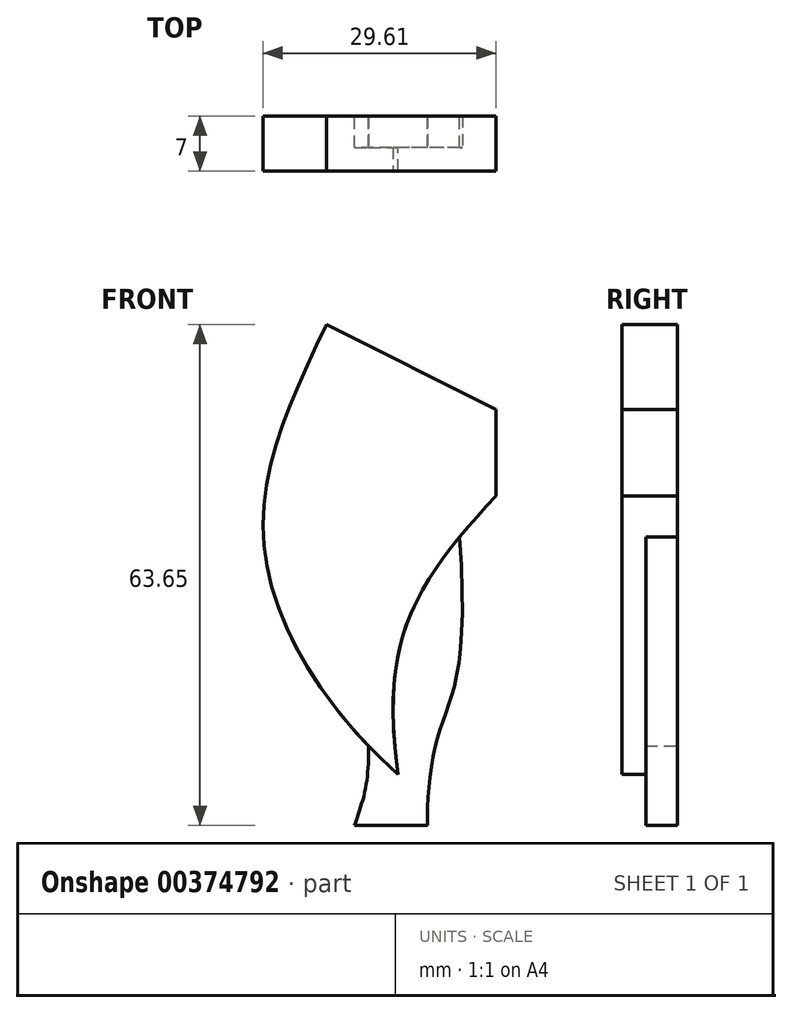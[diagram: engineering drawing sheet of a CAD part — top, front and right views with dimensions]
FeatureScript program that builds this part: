
annotation { "Feature Type Name" : "Feature", "Feature Type Description" : "" }
export const myFeature = defineFeature(function(context is Context, id is Id, definition is map)
    precondition{}
    {
        {
            var Q0;
            Q0=qCreatedBy(makeId("Front.planeOp"),FACE);
            var sketch = newSketch(context, id + "F0", { "sketchPlane" : qUnion([Q0])});
            skLineSegment(sketch, "E0", {"start": v(1.24, 25.64) * mm, "end": v(22.82, 14.85) * mm});
            skLineSegment(sketch, "E1", {"start": v(22.82, 14.85) * mm, "end": v(22.82, 3.84) * mm});
            skFitSpline(sketch, "E2", {"points": [v(1.24, 25.64) * mm, v(-6.63, -2.85) * mm, v(10.35, -31.5) * mm], "startDerivative": vector(-28.14, -59.83) * mm, "endDerivative": vector(50.37, -44.22) * mm});
            skFitSpline(sketch, "E3", {"points": [v(22.82, 3.84) * mm, v(11.92, -11.26) * mm, v(10.35, -31.5) * mm], "startDerivative": vector(-28.02, -29.3) * mm, "endDerivative": vector(6.68, -49.81) * mm});
            skSolve(sketch);
        }
        {
            var Q0;
            Q0 = qSketchRegion(id + "F0", true);
            extrude(context, id + "F1", {"entities" : qUnion([Q0]), "depth" : 7 * mm, "offsetDistance" : 25 * mm});
        }
        {
            var Q0;
            Q0=makeQuery(id+"F1.opExtrude","CAP_FACE",FACE,{"disambiguationData":[OSD([sQuery(id+"F0.wireOp",EDGE,"E0"),sQuery(id+"F0.wireOp",EDGE,"E1"),sQuery(id+"F0.wireOp",EDGE,"E2"),sQuery(id+"F0.wireOp",EDGE,"E3")])],"isStart":true});
            var sketch = newSketch(context, id + "F2", { "sketchPlane" : qUnion([Q0])});
            skFitSpline(sketch, "E4", {"points": [v(-18.16, -1.37) * mm, v(-15.45, -26.61) * mm, v(-14.13, -38.01) * mm], "startDerivative": vector(-6.58, -89.09) * mm, "endDerivative": vector(-1.28, -24.69) * mm});
            skLineSegment(sketch, "E5", {"start": v(-14.13, -38.01) * mm, "end": v(-4.85, -38.01) * mm});
            skFitSpline(sketch, "E6", {"points": [v(-4.85, -38.01) * mm, v(-6.28, -33.05) * mm, v(-6.61, -27.9) * mm], "startDerivative": vector(-2.35, 8.2) * mm, "endDerivative": vector(0.15, 5.37) * mm});
            skSolve(sketch);
        }
        {
            var Q0;
            {var subQ4=sQuery(id+"F2.wireOp",EDGE,"E4");Q0=makeQuery(id+"F2.imprint","IMPRINT",FACE,{"disambiguationData":[TD([[makeQuery(id+"F2.imprint","IMPRINT",EDGE,{"derivedFrom":subQ4}),1.0]])]});}
            extrude(context, id + "F3", {"entities" : qUnion([Q0]), "operationType" : NewBodyOperationType.ADD, "oppositeDirection" : true, "depth" : 4 * mm, "offsetDistance" : 25 * mm});
        }
    });
